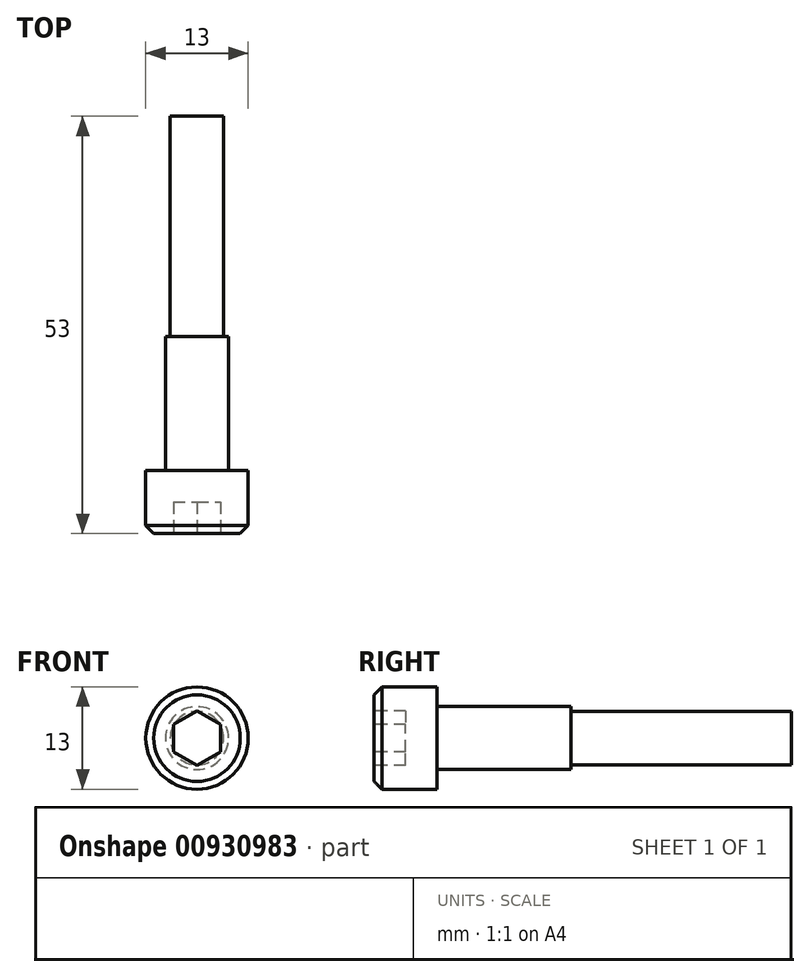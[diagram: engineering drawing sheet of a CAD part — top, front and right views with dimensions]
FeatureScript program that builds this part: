
annotation { "Feature Type Name" : "Feature", "Feature Type Description" : "" }
export const myFeature = defineFeature(function(context is Context, id is Id, definition is map)
    precondition{}
    {
        {
            var Q0;
            Q0=qCreatedBy(makeId("Front.planeOp"),FACE);
            var sketch = newSketch(context, id + "F0", { "sketchPlane" : qUnion([Q0])});
            skCircle(sketch, "E0", {"center": v(0, 0) * mm, "radius": 6.5 * mm});
            skSolve(sketch);
        }
        {
            var Q0;
            Q0 = qSketchRegion(id + "F0", true);
            extrude(context, id + "F1", {"entities" : qUnion([Q0]), "oppositeDirection" : true, "depth" : 8 * mm, "offsetDistance" : 25 * mm});
        }
        {
            var Q0;
            Q0=makeQuery(id+"F1.opExtrude","CAP_FACE",FACE,{"disambiguationData":[OSD([sQuery(id+"F0.wireOp",EDGE,"E0")])],"isStart":true});
            var sketch = newSketch(context, id + "F2", { "sketchPlane" : qUnion([Q0])});
            skCircle(sketch, "E1.cCircle", {"center": v(0, 0) * mm, "radius": 3 * mm, "construction": true});
            skLineSegment(sketch, "E1.0", {"start": v(0, 3.46) * mm, "end": v(3, 1.73) * mm});
            skLineSegment(sketch, "E1.1", {"start": v(3, 1.73) * mm, "end": v(3, -1.73) * mm});
            skLineSegment(sketch, "E1.2", {"start": v(3, -1.73) * mm, "end": v(0, -3.46) * mm});
            skLineSegment(sketch, "E1.3", {"start": v(0, -3.46) * mm, "end": v(-3, -1.73) * mm});
            skLineSegment(sketch, "E1.4", {"start": v(-3, -1.73) * mm, "end": v(-3, 1.73) * mm});
            skLineSegment(sketch, "E1.5", {"start": v(-3, 1.73) * mm, "end": v(0, 3.46) * mm});
            skPoint(sketch, "E1.0.midPoint", {"position": v(1.5, 2.6) * mm});
            skSolve(sketch);
        }
        {
            var Q0;
            Q0 = qSketchRegion(id + "F2", true);
            extrude(context, id + "F3", {"entities" : qUnion([Q0]), "operationType" : NewBodyOperationType.REMOVE, "oppositeDirection" : true, "depth" : 4 * mm, "offsetDistance" : 25 * mm});
        }
        {
            var Q0;
            Q0=makeQuery(id+"F1.opExtrude","CAP_FACE",FACE,{"disambiguationData":[OSD([sQuery(id+"F0.wireOp",EDGE,"E0")])],"isStart":false});
            var sketch = newSketch(context, id + "F4", { "sketchPlane" : qUnion([Q0])});
            skCircle(sketch, "E2", {"center": v(0, 0) * mm, "radius": 4 * mm});
            skSolve(sketch);
        }
        {
            var Q0;
            Q0 = qSketchRegion(id + "F4", true);
            extrude(context, id + "F5", {"entities" : qUnion([Q0]), "operationType" : NewBodyOperationType.ADD, "depth" : 45 * mm, "offsetDistance" : 25 * mm});
        }
        {
            var Q0;
            Q0=makeQuery(id+"F5.opExtrude","CAP_FACE",FACE,{"disambiguationData":[OSD([sQuery(id+"F4.wireOp",EDGE,"E2")])],"isStart":false});
            var sketch = newSketch(context, id + "F6", { "sketchPlane" : qUnion([Q0])});
            skCircle(sketch, "E3", {"center": v(0, 0) * mm, "radius": 3.4 * mm});
            skSolve(sketch);
        }
        {
            var Q0;
            Q0=makeQuery(id+"F6.imprint","IMPRINT",FACE,{"disambiguationData":[TD([[makeQuery(id+"F6.imprint","IMPRINT",EDGE,{"derivedFrom":sQuery(id+"F6.wireOp",EDGE,"E3")}),-1.0]])]});
            extrude(context, id + "F7", {"entities" : qUnion([Q0]), "operationType" : NewBodyOperationType.REMOVE, "oppositeDirection" : true, "depth" : 28 * mm, "offsetDistance" : 25 * mm});
        }
        {
            var Q0;
            Q0=makeQuery(id+"F1.opExtrude","CAP_EDGE",EDGE,{"disambiguationData":[OSD([sQuery(id+"F0.wireOp",EDGE,"E0")])],"isStart":true});
            chamfer(context, id + "F8", {"entities" : qUnion([Q0]), "width" : 1 * mm, "tangentPropagation" : true});
        }
    });
